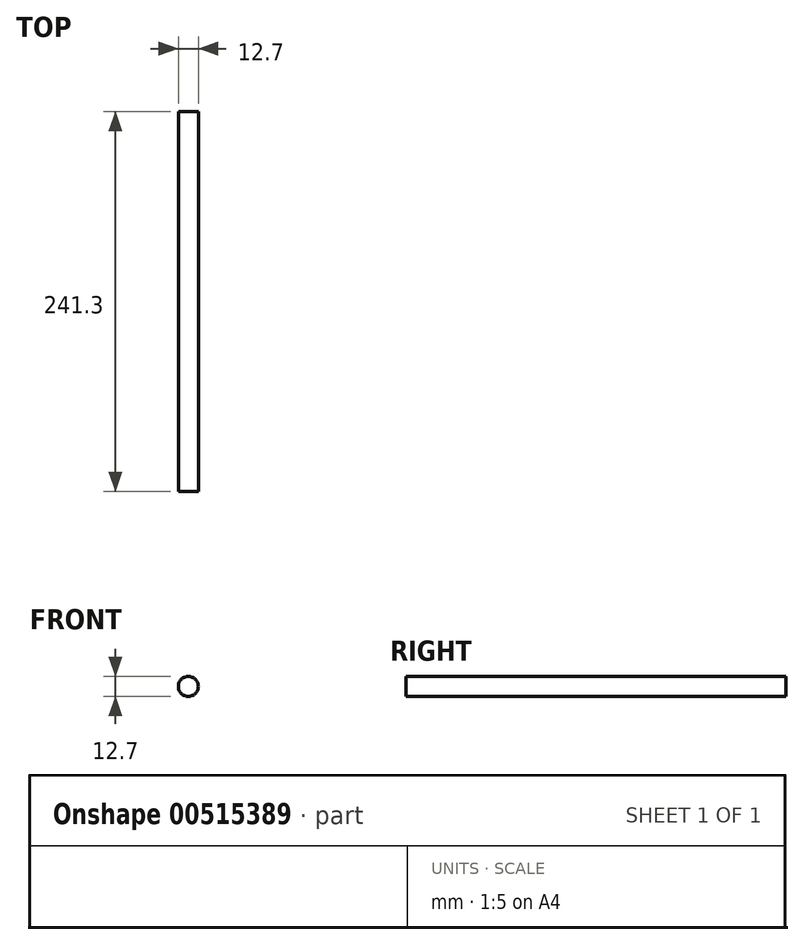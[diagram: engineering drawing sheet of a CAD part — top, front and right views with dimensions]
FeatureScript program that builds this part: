
annotation { "Feature Type Name" : "Feature", "Feature Type Description" : "" }
export const myFeature = defineFeature(function(context is Context, id is Id, definition is map)
    precondition{}
    {
        {
            var Q0;
            Q0=qCreatedBy(makeId("Front.planeOp"),FACE);
            var sketch = newSketch(context, id + "F0", { "sketchPlane" : qUnion([Q0])});
            skCircle(sketch, "E0", {"center": v(0, 0) * mm, "radius": 6.35 * mm});
            skSolve(sketch);
        }
        {
            var Q0;
            Q0=makeQuery(id+"F0.imprint","IMPRINT",FACE,{"disambiguationData":[TD([[makeQuery(id+"F0.imprint","IMPRINT",EDGE,{"derivedFrom":sQuery(id+"F0.wireOp",EDGE,"E0")}),1.0]])]});
            extrude(context, id + "F1", {"entities" : qUnion([Q0]), "depth" : 241.3 * mm, "offsetDistance" : 25.4 * mm});
        }
    });
